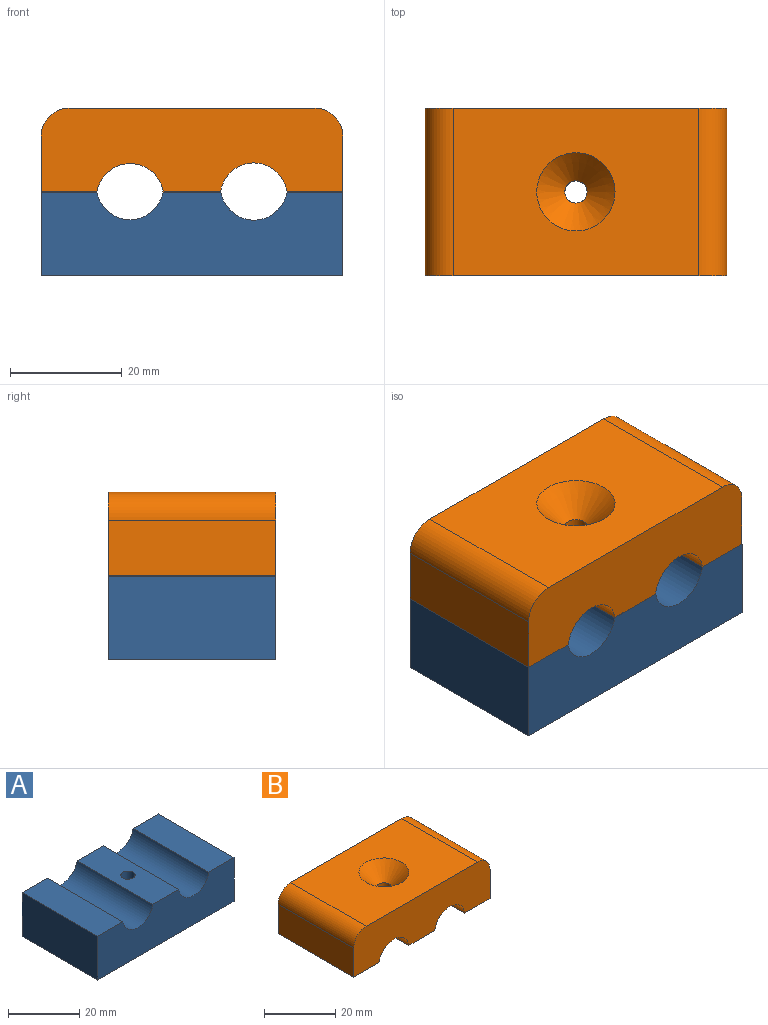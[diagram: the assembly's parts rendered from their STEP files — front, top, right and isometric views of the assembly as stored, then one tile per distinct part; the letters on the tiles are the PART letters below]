
ASSEMBLY  parts=2 mates=1
PART A: 11 faces, bbox 54x30x15 mm
  f0: plane 30x10mm, normal (0,0,1), area 300mm2, adj f5,f6,f7,f9
  f1: plane 30x10.35mm, normal (0,0,1), area 297.9mm2, adj f6,f7,f8,f9,f10
  f2: plane 54x30mm, normal (0,0,-1), area 1607.4mm2, adj f3,f5,f6,f7,f10
  f3: plane 30x15mm, normal (1,0,0), area 450mm2, adj f2,f4,f6,f7
  f4: plane 30x10mm, normal (0,0,1), area 300mm2, adj f3,f6,f7,f8
  f5: plane 30x15mm, normal (-1,0,0), area 450mm2, adj f0,f2,f6,f7
  f6: plane 54x15mm, normal (0,-1,0), area 721.2mm2, adj f0,f1,f2,f3,f4,f5,f8,f9
  f7: plane 54x15mm, normal (0,1,0), area 721.2mm2, adj f0,f1,f2,f3,f4,f5,f8,f9
  f8: cylinder r=6mm len=30mm, axis (0,-1,0), area 506.7mm2, adj f1,f4,f6,f7
  f9: cylinder r=6mm len=30mm, axis (0,-1,0), area 501.5mm2, adj f0,f1,f6,f7
  f10: cylinder r=2mm len=15mm, axis (0,0,1), area 188.5mm2, adj f1,f2
PART B: 14 faces, bbox 54x30x15 mm
  f0: plane 30x10.25mm, normal (0,0,-1), area 294.8mm2, adj f6,f7,f8,f9,f10
  f1: plane 30x10mm, normal (0,0,-1), area 300mm2, adj f5,f6,f7,f8
  f2: plane 44x30mm, normal (0,0,1), area 1166.1mm2, adj f6,f7,f11,f12,f13
  f3: plane 30x10mm, normal (-1,0,0), area 300mm2, adj f4,f6,f7,f12
  f4: plane 30x10mm, normal (0,0,-1), area 300mm2, adj f3,f6,f7,f9
  f5: plane 30x10mm, normal (1,0,0), area 300mm2, adj f1,f6,f7,f13
  f6: plane 54x15mm, normal (0,-1,0), area 706.6mm2, adj f0,f1,f2,f3,f4,f5,f8,f9
  f7: plane 54x15mm, normal (0,1,0), area 706.6mm2, adj f0,f1,f2,f3,f4,f5,f8,f9
  f8: cylinder r=6mm len=30mm, axis (0,-1,0), area 517.8mm2, adj f0,f1,f6,f7
  f9: cylinder r=6mm len=30mm, axis (0,-1,0), area 510.3mm2, adj f0,f4,f6,f7
  f10: cylinder r=2mm len=10mm, axis (0,0,-1), area 125.7mm2, adj f0,f11
  f11: cone r=7mm half-angle=45deg, axis (0,0,1), area 199.9mm2, adj f2,f10
  f12: cylinder r=5mm len=30mm, axis (0,-1,0), area 235.6mm2, adj f2,f3,f6,f7
  f13: cylinder r=5mm len=30mm, axis (0,1,0), area 235.6mm2, adj f2,f5,f6,f7
PLACE A t=(-28.69,-8.19,-9.94)mm
PLACE B t=(-1.69,-8.19,-25.12)mm
MATE planar B.f4 <-> A.f0  axis (0,0,1) through (-55.69,-38.19,-2.44)mm
